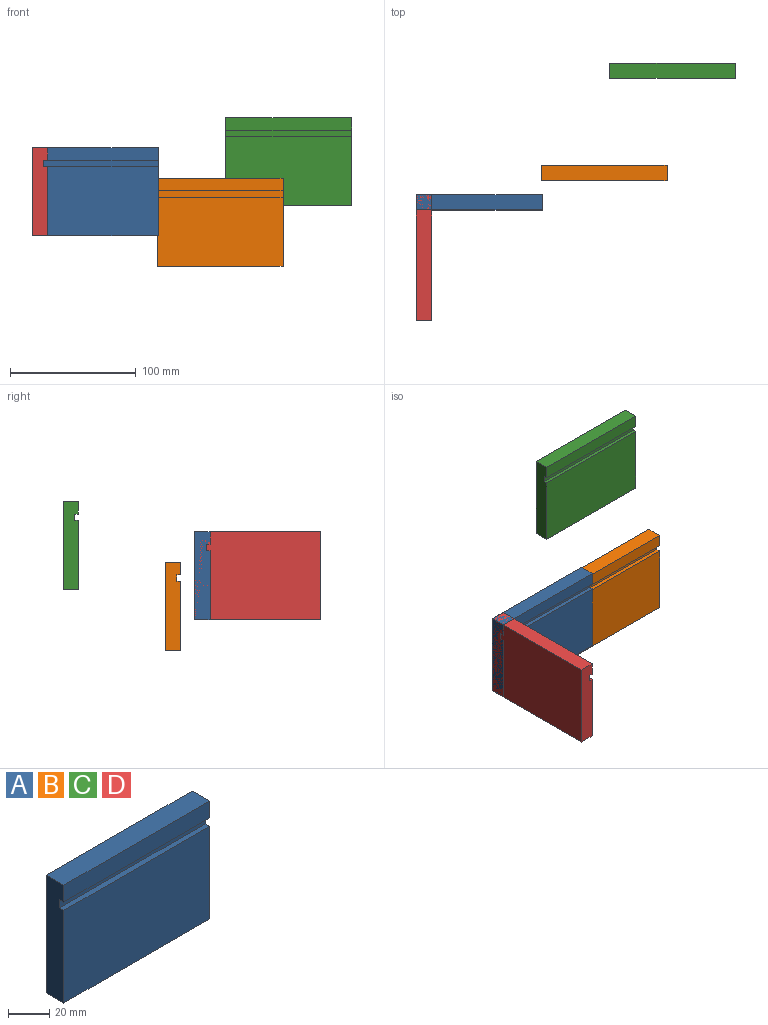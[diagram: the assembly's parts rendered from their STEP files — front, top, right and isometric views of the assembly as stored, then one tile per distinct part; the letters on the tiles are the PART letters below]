
ASSEMBLY  parts=4 mates=1
PART A: 10 faces, bbox 100x12x70 mm
  f0: plane 100x70mm, normal (0,1,0), area 7000mm2, adj f1,f6,f8,f9
  f1: plane 100x12mm, normal (0,0,1), area 1200mm2, adj f0,f7,f8,f9
  f2: plane 100x3mm, normal (0,0,-1), area 300mm2, adj f3,f7,f8,f9
  f3: plane 100x5mm, normal (0,-1,0), area 500mm2, adj f2,f4,f8,f9
  f4: plane 100x3mm, normal (0,0,1), area 300mm2, adj f3,f5,f8,f9
  f5: plane 100x55mm, normal (0,-1,0), area 5500mm2, adj f4,f6,f8,f9
  f6: plane 100x12mm, normal (0,0,-1), area 1200mm2, adj f0,f5,f8,f9
  f7: plane 100x10mm, normal (0,-1,0), area 1000mm2, adj f1,f2,f8,f9
  f8: plane 70x12mm, normal (-1,0,0), area 825mm2, adj f0,f1,f2,f3,f4,f5,f6,f7
  f9: plane 70x12mm, normal (1,0,0), area 825mm2, adj f0,f1,f2,f3,f4,f5,f6,f7
PART B: same geometry as A
PART C: same geometry as A
PART D: same geometry as A
PLACE A t=(-2.62,-22.63,-31.68)mm
PLACE B t=(96.45,0.79,-56.01)mm
PLACE C t=(150.89,81.99,-7.69)mm
PLACE D rot(axis=(0,0,1),90deg) t=(-2.62,-122.63,-31.68)mm
MATE fastened D.f1 <-> A.f1  axis (0,0,1) through (-2.62,-22.63,38.32)mm
